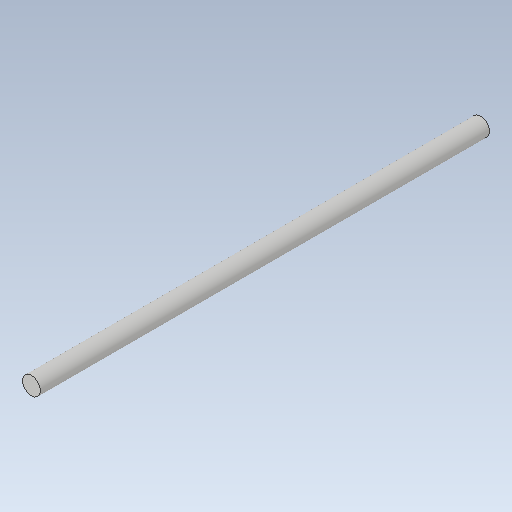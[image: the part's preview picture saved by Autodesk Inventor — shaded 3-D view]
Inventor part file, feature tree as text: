
AUTODESK INVENTOR PART (.ipt)
format: ipt  version: 2020.1 (Build 241239000, 239)  size: 80,896 bytes
history: native  units: mm
features: extrude x1, sketch x1
ambient origin geometry x8: Origin, YZ Plane, XZ Plane, XY Plane, X Axis, Y Axis, Z Axis, Center Point
bodies: Solid1 (feature_tree)
feature tree (2):
  extrude  "Extrusion1"  Depth=250.0mm TaperAngle=0.0deg
  sketch  "Sketch1"  dims[d0=10.0mm d1=250.0mm d2=0.0mm]
